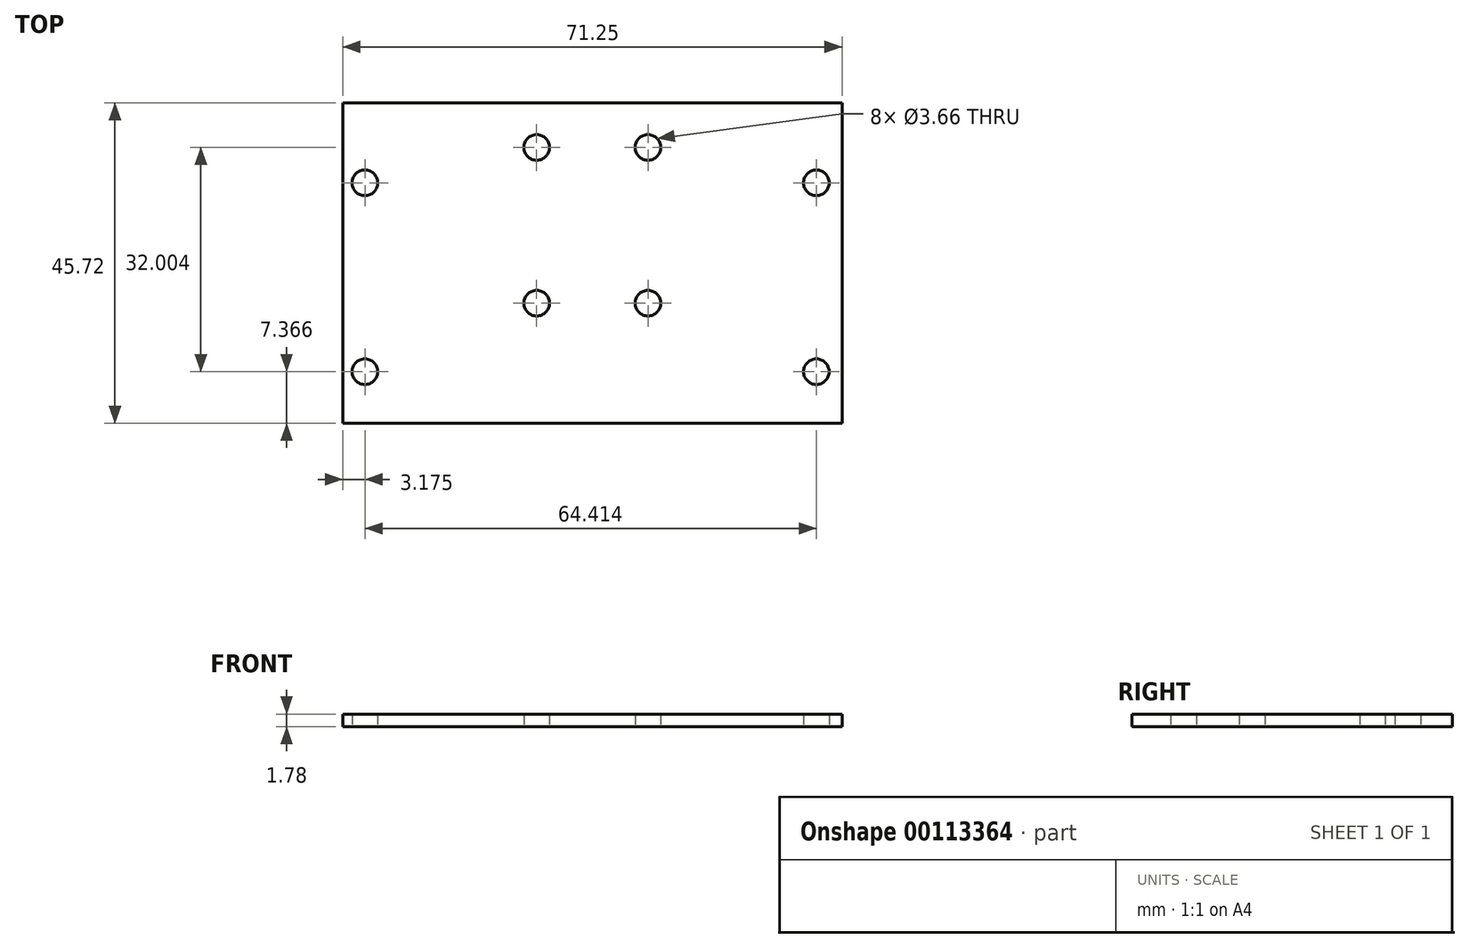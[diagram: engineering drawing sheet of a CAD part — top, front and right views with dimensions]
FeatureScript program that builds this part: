
annotation { "Feature Type Name" : "Feature", "Feature Type Description" : "" }
export const myFeature = defineFeature(function(context is Context, id is Id, definition is map)
    precondition{}
    {
        {
            var Q0;
            Q0=qCreatedBy(makeId("Top.planeOp"),FACE);
            var sketch = newSketch(context, id + "F0", { "sketchPlane" : qUnion([Q0])});
            skLineSegment(sketch, "E0.bottom", {"start": v(0, 0) * mm, "end": v(71.25, 0) * mm});
            skLineSegment(sketch, "E0.top", {"start": v(0, 45.72) * mm, "end": v(71.25, 45.72) * mm});
            skLineSegment(sketch, "E0.left", {"start": v(0, 0) * mm, "end": v(0, 45.72) * mm});
            skLineSegment(sketch, "E0.right", {"start": v(71.25, 0) * mm, "end": v(71.25, 45.72) * mm});
            skCircle(sketch, "E1", {"center": v(3.17, 7.37) * mm, "radius": 1.83 * mm});
            skCircle(sketch, "E2", {"center": v(3.17, 34.32) * mm, "radius": 1.83 * mm});
            skCircle(sketch, "E3", {"center": v(67.59, 34.32) * mm, "radius": 1.83 * mm});
            skCircle(sketch, "E4", {"center": v(67.59, 7.37) * mm, "radius": 1.83 * mm});
            skCircle(sketch, "E5", {"center": v(27.69, 17.15) * mm, "radius": 1.83 * mm});
            skCircle(sketch, "E6", {"center": v(27.69, 39.37) * mm, "radius": 1.83 * mm});
            skCircle(sketch, "E7", {"center": v(43.56, 39.37) * mm, "radius": 1.83 * mm});
            skCircle(sketch, "E8", {"center": v(43.56, 17.15) * mm, "radius": 1.83 * mm});
            skLineSegment(sketch, "E9", {"start": v(6.35, 0) * mm, "end": v(6.35, 45.72) * mm, "construction": true});
            skLineSegment(sketch, "E10", {"start": v(64.9, 45.72) * mm, "end": v(64.9, 0) * mm, "construction": true});
            skLineSegment(sketch, "E11", {"start": v(8.64, 45.72) * mm, "end": v(8.64, 0) * mm, "construction": true});
            skLineSegment(sketch, "E12", {"start": v(62.61, 45.72) * mm, "end": v(62.61, 0) * mm, "construction": true});
            skSolve(sketch);
        }
        {
            var Q0;
            Q0=makeQuery(id+"F0.imprint","IMPRINT",FACE,{"disambiguationData":[TD([[makeQuery(id+"F0.imprint","IMPRINT",EDGE,{"derivedFrom":sQuery(id+"F0.wireOp",EDGE,"E0.bottom")}),1.0]])]});
            extrude(context, id + "F1", {"entities" : qUnion([Q0]), "depth" : 1.78 * mm, "offsetDistance" : 25.4 * mm});
        }
    });
